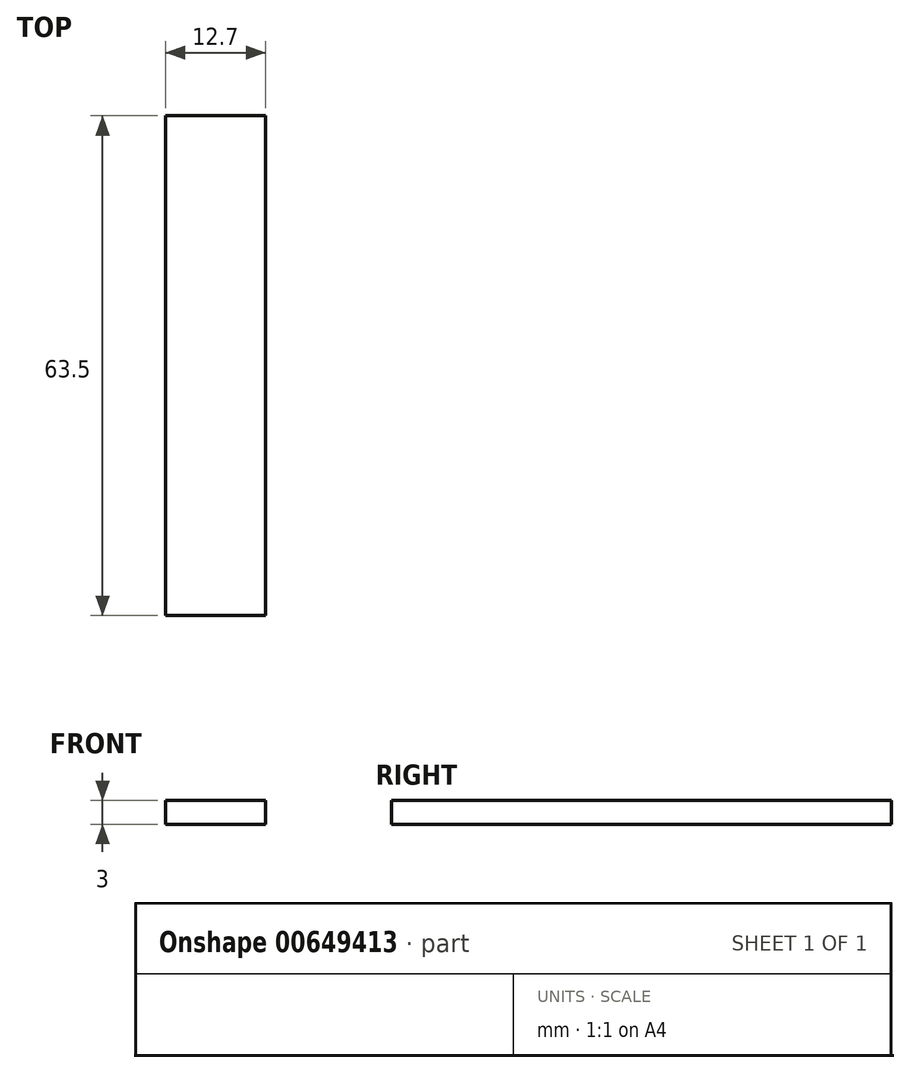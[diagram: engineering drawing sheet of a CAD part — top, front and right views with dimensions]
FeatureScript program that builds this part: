
annotation { "Feature Type Name" : "Feature", "Feature Type Description" : "" }
export const myFeature = defineFeature(function(context is Context, id is Id, definition is map)
    precondition{}
    {
        {
            var Q0;
            Q0=qCreatedBy(makeId("Top.planeOp"),FACE);
            var sketch = newSketch(context, id + "F0", { "sketchPlane" : qUnion([Q0])});
            skLineSegment(sketch, "E0.bottom", {"start": v(0, 0) * mm, "end": v(12.7, 0) * mm});
            skLineSegment(sketch, "E0.top", {"start": v(0, 63.5) * mm, "end": v(12.7, 63.5) * mm});
            skLineSegment(sketch, "E0.left", {"start": v(0, 0) * mm, "end": v(0, 63.5) * mm});
            skLineSegment(sketch, "E0.right", {"start": v(12.7, 0) * mm, "end": v(12.7, 63.5) * mm});
            skSolve(sketch);
        }
        {
            var Q0;
            Q0 = qSketchRegion(id + "F0", true);
            extrude(context, id + "F1", {"entities" : qUnion([Q0]), "depth" : 3 * mm, "offsetDistance" : 25.4 * mm});
        }
    });
